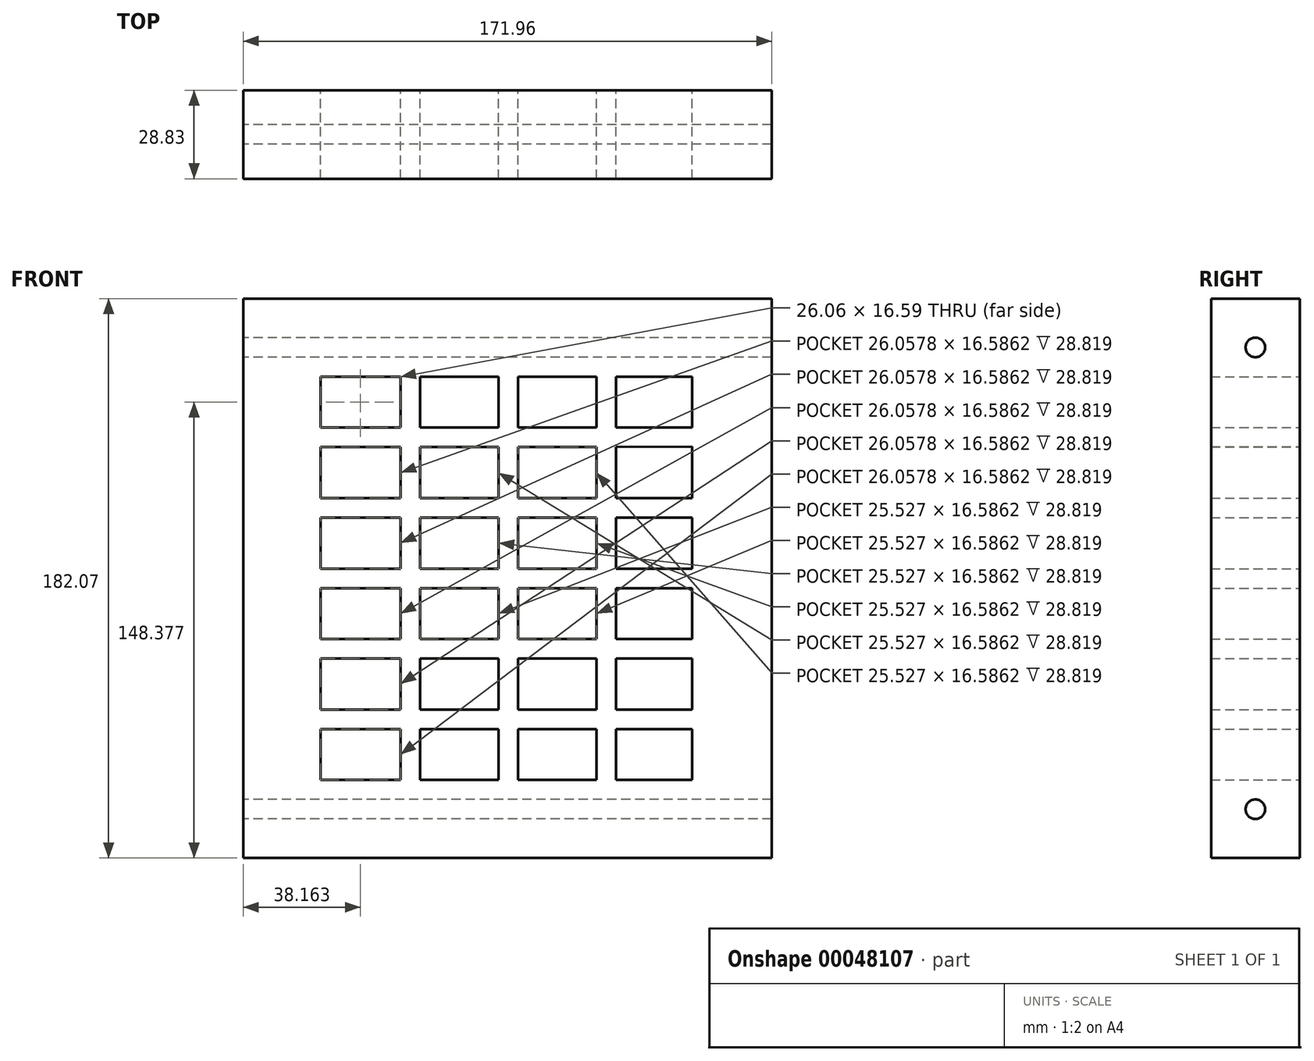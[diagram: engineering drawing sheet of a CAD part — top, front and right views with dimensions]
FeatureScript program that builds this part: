
annotation { "Feature Type Name" : "Feature", "Feature Type Description" : "" }
export const myFeature = defineFeature(function(context is Context, id is Id, definition is map)
    precondition{}
    {
        {
            var Q0;
            Q0=qCreatedBy(makeId("Front.planeOp"),FACE);
            var sketch = newSketch(context, id + "F0", { "sketchPlane" : qUnion([Q0])});
            skLineSegment(sketch, "E0", {"start": v(0, 0) * mm, "end": v(0, -182.07) * mm});
            skLineSegment(sketch, "E1", {"start": v(0, 0) * mm, "end": v(171.96, 0) * mm});
            skLineSegment(sketch, "E2", {"start": v(171.96, 0) * mm, "end": v(171.96, -182.07) * mm});
            skLineSegment(sketch, "E3", {"start": v(171.96, -182.07) * mm, "end": v(0, -182.07) * mm});
            skLineSegment(sketch, "E4", {"start": v(25.13, -25.4) * mm, "end": v(146.03, -25.4) * mm});
            skLineSegment(sketch, "E5.bottom", {"start": v(25.13, -25.4) * mm, "end": v(51.2, -25.4) * mm});
            skLineSegment(sketch, "E5.left", {"start": v(25.13, -25.4) * mm, "end": v(25.13, -41.46) * mm});
            skLineSegment(sketch, "E6", {"start": v(25.13, -25.4) * mm, "end": v(25.13, -41.99) * mm});
            skLineSegment(sketch, "E7", {"start": v(38.16, -48.34) * mm, "end": v(25.13, -48.34) * mm});
            skLineSegment(sketch, "E8", {"start": v(25.13, -48.34) * mm, "end": v(51.2, -48.34) * mm});
            skLineSegment(sketch, "E9", {"start": v(25.13, -48.34) * mm, "end": v(25.13, -64.92) * mm});
            skLineSegment(sketch, "E10", {"start": v(25.13, -41.99) * mm, "end": v(25.13, -48.34) * mm});
            skLineSegment(sketch, "E11", {"start": v(25.13, -64.92) * mm, "end": v(51.2, -64.92) * mm});
            skLineSegment(sketch, "E12", {"start": v(51.2, -64.92) * mm, "end": v(38.16, -64.92) * mm});
            skLineSegment(sketch, "E13", {"start": v(38.16, -71.27) * mm, "end": v(25.13, -71.27) * mm});
            skLineSegment(sketch, "E14", {"start": v(25.13, -71.27) * mm, "end": v(25.13, -87.86) * mm});
            skLineSegment(sketch, "E15", {"start": v(38.16, -71.27) * mm, "end": v(51.2, -71.27) * mm});
            skLineSegment(sketch, "E16", {"start": v(25.13, -87.86) * mm, "end": v(51.2, -87.86) * mm});
            skLineSegment(sketch, "E17", {"start": v(51.2, -87.86) * mm, "end": v(38.16, -87.86) * mm});
            skLineSegment(sketch, "E18", {"start": v(38.16, -94.2) * mm, "end": v(25.13, -94.2) * mm});
            skLineSegment(sketch, "E19", {"start": v(25.13, -94.2) * mm, "end": v(25.13, -110.8) * mm});
            skLineSegment(sketch, "E20", {"start": v(25.13, -110.8) * mm, "end": v(51.2, -110.8) * mm});
            skLineSegment(sketch, "E21", {"start": v(38.16, -94.2) * mm, "end": v(51.2, -94.2) * mm});
            skLineSegment(sketch, "E22", {"start": v(51.2, -94.2) * mm, "end": v(51.2, -110.8) * mm});
            skLineSegment(sketch, "E23", {"start": v(38.16, -117.14) * mm, "end": v(25.13, -117.14) * mm});
            skLineSegment(sketch, "E24", {"start": v(25.13, -117.14) * mm, "end": v(51.2, -117.14) * mm});
            skLineSegment(sketch, "E25", {"start": v(25.13, -117.14) * mm, "end": v(25.13, -133.73) * mm});
            skLineSegment(sketch, "E26", {"start": v(25.13, -133.73) * mm, "end": v(51.2, -133.73) * mm});
            skLineSegment(sketch, "E27", {"start": v(51.2, -133.73) * mm, "end": v(38.16, -133.73) * mm});
            skLineSegment(sketch, "E28", {"start": v(38.16, -140.08) * mm, "end": v(25.13, -140.08) * mm});
            skLineSegment(sketch, "E29", {"start": v(25.13, -140.08) * mm, "end": v(25.13, -156.67) * mm});
            skLineSegment(sketch, "E30", {"start": v(38.16, -140.08) * mm, "end": v(51.2, -140.08) * mm});
            skLineSegment(sketch, "E31", {"start": v(25.13, -25.4) * mm, "end": v(25.13, -156.67) * mm});
            skPoint(sketch, "E32.endSnap0", {"position": v(171.96, -91.03) * mm});
            skLineSegment(sketch, "E33", {"start": v(51.2, -25.4) * mm, "end": v(85.58, -25.4) * mm});
            skLineSegment(sketch, "E34", {"start": v(146.03, -25.4) * mm, "end": v(146.03, -156.67) * mm});
            skLineSegment(sketch, "E35", {"start": v(25.13, -156.67) * mm, "end": v(146.03, -156.67) * mm});
            skLineSegment(sketch, "E36", {"start": v(57.54, -140.08) * mm, "end": v(83.07, -140.08) * mm});
            skLineSegment(sketch, "E37", {"start": v(89.42, -140.08) * mm, "end": v(114.95, -140.08) * mm});
            skLineSegment(sketch, "E38", {"start": v(121.3, -140.08) * mm, "end": v(146.03, -140.08) * mm});
            skLineSegment(sketch, "E39", {"start": v(57.54, -117.14) * mm, "end": v(83.07, -117.14) * mm});
            skLineSegment(sketch, "E40", {"start": v(89.42, -117.14) * mm, "end": v(114.95, -117.14) * mm});
            skLineSegment(sketch, "E41", {"start": v(121.3, -117.14) * mm, "end": v(146.03, -117.14) * mm});
            skLineSegment(sketch, "E42", {"start": v(57.54, -94.2) * mm, "end": v(83.07, -94.2) * mm});
            skLineSegment(sketch, "E43", {"start": v(89.42, -94.2) * mm, "end": v(114.95, -94.2) * mm});
            skLineSegment(sketch, "E44", {"start": v(121.3, -94.2) * mm, "end": v(146.03, -94.2) * mm});
            skLineSegment(sketch, "E45", {"start": v(57.54, -87.86) * mm, "end": v(83.07, -87.86) * mm});
            skLineSegment(sketch, "E46", {"start": v(89.42, -87.86) * mm, "end": v(114.95, -87.86) * mm});
            skLineSegment(sketch, "E47", {"start": v(121.3, -87.86) * mm, "end": v(146.03, -87.86) * mm});
            skLineSegment(sketch, "E48", {"start": v(57.54, -71.27) * mm, "end": v(83.07, -71.27) * mm});
            skLineSegment(sketch, "E49", {"start": v(89.42, -71.27) * mm, "end": v(114.95, -71.27) * mm});
            skLineSegment(sketch, "E50", {"start": v(121.3, -71.27) * mm, "end": v(146.03, -71.27) * mm});
            skLineSegment(sketch, "E51", {"start": v(57.54, -110.8) * mm, "end": v(83.07, -110.8) * mm});
            skLineSegment(sketch, "E52", {"start": v(89.42, -110.8) * mm, "end": v(114.95, -110.8) * mm});
            skLineSegment(sketch, "E53", {"start": v(121.3, -110.8) * mm, "end": v(146.03, -110.8) * mm});
            skLineSegment(sketch, "E54", {"start": v(57.54, -133.73) * mm, "end": v(83.07, -133.73) * mm});
            skLineSegment(sketch, "E55", {"start": v(89.42, -133.73) * mm, "end": v(114.95, -133.73) * mm});
            skLineSegment(sketch, "E56", {"start": v(121.3, -133.73) * mm, "end": v(146.03, -133.73) * mm});
            skLineSegment(sketch, "E57", {"start": v(57.54, -64.92) * mm, "end": v(83.07, -64.92) * mm});
            skLineSegment(sketch, "E58", {"start": v(89.42, -64.92) * mm, "end": v(114.95, -64.92) * mm});
            skLineSegment(sketch, "E59", {"start": v(121.3, -64.92) * mm, "end": v(146.03, -64.92) * mm});
            skLineSegment(sketch, "E60", {"start": v(57.54, -48.34) * mm, "end": v(83.07, -48.34) * mm});
            skLineSegment(sketch, "E61", {"start": v(89.42, -48.34) * mm, "end": v(114.95, -48.34) * mm});
            skLineSegment(sketch, "E62", {"start": v(121.3, -48.34) * mm, "end": v(146.03, -48.2) * mm});
            skLineSegment(sketch, "E63", {"start": v(57.54, -41.99) * mm, "end": v(83.07, -41.99) * mm});
            skLineSegment(sketch, "E64", {"start": v(89.42, -41.99) * mm, "end": v(114.95, -41.99) * mm});
            skLineSegment(sketch, "E65", {"start": v(121.3, -41.99) * mm, "end": v(146.03, -41.99) * mm});
            skLineSegment(sketch, "E66", {"start": v(51.2, -140.08) * mm, "end": v(51.2, -156.67) * mm});
            skLineSegment(sketch, "E67", {"start": v(51.2, -117.14) * mm, "end": v(51.2, -133.73) * mm});
            skLineSegment(sketch, "E68", {"start": v(51.2, -87.86) * mm, "end": v(51.2, -71.27) * mm});
            skLineSegment(sketch, "E69", {"start": v(51.2, -64.92) * mm, "end": v(51.2, -48.34) * mm});
            skLineSegment(sketch, "E70", {"start": v(57.54, -41.99) * mm, "end": v(57.54, -25.4) * mm});
            skLineSegment(sketch, "E71", {"start": v(57.54, -48.34) * mm, "end": v(57.54, -64.92) * mm});
            skLineSegment(sketch, "E72", {"start": v(57.54, -71.27) * mm, "end": v(57.54, -87.86) * mm});
            skLineSegment(sketch, "E73", {"start": v(57.54, -94.2) * mm, "end": v(57.54, -110.8) * mm});
            skLineSegment(sketch, "E74", {"start": v(57.54, -117.14) * mm, "end": v(57.54, -133.73) * mm});
            skLineSegment(sketch, "E75", {"start": v(57.54, -140.08) * mm, "end": v(57.54, -156.67) * mm});
            skLineSegment(sketch, "E76", {"start": v(83.07, -140.08) * mm, "end": v(83.07, -156.67) * mm});
            skLineSegment(sketch, "E77", {"start": v(83.07, -133.73) * mm, "end": v(83.07, -117.14) * mm});
            skLineSegment(sketch, "E78", {"start": v(83.07, -110.8) * mm, "end": v(83.07, -94.2) * mm});
            skLineSegment(sketch, "E79", {"start": v(83.07, -87.86) * mm, "end": v(83.07, -71.27) * mm});
            skLineSegment(sketch, "E80", {"start": v(83.07, -64.92) * mm, "end": v(83.07, -48.34) * mm});
            skLineSegment(sketch, "E81", {"start": v(83.07, -41.99) * mm, "end": v(83.07, -25.4) * mm});
            skLineSegment(sketch, "E82", {"start": v(89.42, -41.99) * mm, "end": v(89.42, -25.4) * mm});
            skLineSegment(sketch, "E83", {"start": v(89.42, -48.34) * mm, "end": v(89.42, -64.92) * mm});
            skLineSegment(sketch, "E84", {"start": v(89.42, -87.86) * mm, "end": v(89.42, -71.27) * mm});
            skLineSegment(sketch, "E85", {"start": v(89.42, -94.2) * mm, "end": v(89.42, -110.8) * mm});
            skLineSegment(sketch, "E86", {"start": v(89.42, -117.14) * mm, "end": v(89.42, -133.73) * mm});
            skLineSegment(sketch, "E87", {"start": v(89.42, -140.08) * mm, "end": v(89.42, -156.67) * mm});
            skLineSegment(sketch, "E88", {"start": v(114.95, -140.08) * mm, "end": v(114.95, -156.67) * mm});
            skLineSegment(sketch, "E89", {"start": v(114.95, -133.73) * mm, "end": v(114.95, -117.14) * mm});
            skLineSegment(sketch, "E90", {"start": v(114.95, -110.8) * mm, "end": v(114.95, -94.2) * mm});
            skLineSegment(sketch, "E91", {"start": v(114.95, -87.86) * mm, "end": v(114.95, -71.27) * mm});
            skLineSegment(sketch, "E92", {"start": v(114.95, -64.92) * mm, "end": v(114.95, -48.34) * mm});
            skLineSegment(sketch, "E93", {"start": v(114.95, -41.99) * mm, "end": v(114.95, -25.4) * mm});
            skLineSegment(sketch, "E94", {"start": v(121.3, -41.99) * mm, "end": v(121.3, -25.4) * mm});
            skLineSegment(sketch, "E95", {"start": v(121.3, -48.34) * mm, "end": v(121.3, -64.92) * mm});
            skLineSegment(sketch, "E96", {"start": v(121.3, -71.27) * mm, "end": v(121.3, -87.86) * mm});
            skLineSegment(sketch, "E97", {"start": v(121.3, -94.2) * mm, "end": v(121.3, -110.8) * mm});
            skLineSegment(sketch, "E98", {"start": v(121.3, -117.14) * mm, "end": v(121.3, -133.73) * mm});
            skLineSegment(sketch, "E99", {"start": v(121.3, -140.08) * mm, "end": v(121.3, -156.67) * mm});
            skLineSegment(sketch, "E100", {"start": v(25.13, -41.99) * mm, "end": v(51.2, -41.99) * mm});
            skLineSegment(sketch, "E101", {"start": v(51.2, -41.99) * mm, "end": v(51.2, -25.4) * mm});
            skSolve(sketch);
        }
        {
            var Q0;
            Q0=makeQuery(id+"F0.imprint","IMPRINT",FACE,{"disambiguationData":[TD([[makeQuery(id+"F0.imprint","IMPRINT",EDGE,{"derivedFrom":sQuery(id+"F0.wireOp",EDGE,"E0")}),1.0]])]});
            var Q1;
            {var subQ22=sQuery(id+"F0.wireOp",EDGE,"E11");Q1=makeQuery(id+"F0.imprint","IMPRINT",FACE,{"disambiguationData":[TD([[makeQuery(id+"F0.imprint","IMPRINT",EDGE,{"derivedFrom":subQ22}),-1.0]])]});}
            var Q2;
            Q2=qCreatedBy(makeId("Front.planeOp"),FACE);
            extrude(context, id + "F1", {"entities" : qUnion([Q0, Q1]), "endBoundEntityFace" : qUnion([Q2]), "depth" : 28.83 * mm});
        }
        {
            var Q0;
            {var subQ2=sQuery(id+"F0.wireOp",EDGE,"E5.bottom");Q0=makeQuery(id+"F0.imprint","IMPRINT",FACE,{"disambiguationData":[TD([[makeQuery(id+"F0.imprint","IMPRINT",EDGE,{"derivedFrom":subQ2}),-1.0]])]});}
            var Q1;
            Q1=makeQuery(id+"F0.imprint","IMPRINT",FACE,{"disambiguationData":[TD([[makeQuery(id+"F0.imprint","IMPRINT",EDGE,{"derivedFrom":sQuery(id+"F0.wireOp",EDGE,"E63")}),1.0]])]});
            var Q2;
            Q2=makeQuery(id+"F0.imprint","IMPRINT",FACE,{"disambiguationData":[TD([[makeQuery(id+"F0.imprint","IMPRINT",EDGE,{"derivedFrom":sQuery(id+"F0.wireOp",EDGE,"E64")}),1.0]])]});
            var Q3;
            {var subQ0=sQuery(id+"F0.wireOp",EDGE,"E65");Q3=makeQuery(id+"F0.imprint","IMPRINT",FACE,{"disambiguationData":[TD([[makeQuery(id+"F0.imprint","IMPRINT",EDGE,{"derivedFrom":subQ0}),1.0]])]});}
            var Q4;
            {var subQ1=sQuery(id+"F0.wireOp",EDGE,"E59");Q4=makeQuery(id+"F0.imprint","IMPRINT",FACE,{"disambiguationData":[TD([[makeQuery(id+"F0.imprint","IMPRINT",EDGE,{"derivedFrom":subQ1}),1.0]])]});}
            var Q5;
            Q5=makeQuery(id+"F0.imprint","IMPRINT",FACE,{"disambiguationData":[TD([[makeQuery(id+"F0.imprint","IMPRINT",EDGE,{"derivedFrom":sQuery(id+"F0.wireOp",EDGE,"E58")}),1.0]])]});
            var Q6;
            Q6=makeQuery(id+"F0.imprint","IMPRINT",FACE,{"disambiguationData":[TD([[makeQuery(id+"F0.imprint","IMPRINT",EDGE,{"derivedFrom":sQuery(id+"F0.wireOp",EDGE,"E57")}),1.0]])]});
            var Q7;
            {var subQ5=sQuery(id+"F0.wireOp",EDGE,"E11");Q7=makeQuery(id+"F0.imprint","IMPRINT",FACE,{"disambiguationData":[TD([[makeQuery(id+"F0.imprint","IMPRINT",EDGE,{"derivedFrom":subQ5}),1.0]])]});}
            var Q8;
            {var subQ2=sQuery(id+"F0.wireOp",EDGE,"E13");Q8=makeQuery(id+"F0.imprint","IMPRINT",FACE,{"disambiguationData":[TD([[makeQuery(id+"F0.imprint","IMPRINT",EDGE,{"derivedFrom":subQ2}),1.0]])]});}
            var Q9;
            Q9=makeQuery(id+"F0.imprint","IMPRINT",FACE,{"disambiguationData":[TD([[makeQuery(id+"F0.imprint","IMPRINT",EDGE,{"derivedFrom":sQuery(id+"F0.wireOp",EDGE,"E45")}),1.0]])]});
            var Q10;
            Q10=makeQuery(id+"F0.imprint","IMPRINT",FACE,{"disambiguationData":[TD([[makeQuery(id+"F0.imprint","IMPRINT",EDGE,{"derivedFrom":sQuery(id+"F0.wireOp",EDGE,"E46")}),1.0]])]});
            var Q11;
            {var subQ1=sQuery(id+"F0.wireOp",EDGE,"E47");Q11=makeQuery(id+"F0.imprint","IMPRINT",FACE,{"disambiguationData":[TD([[makeQuery(id+"F0.imprint","IMPRINT",EDGE,{"derivedFrom":subQ1}),1.0]])]});}
            var Q12;
            {var subQ1=sQuery(id+"F0.wireOp",EDGE,"E44");Q12=makeQuery(id+"F0.imprint","IMPRINT",FACE,{"disambiguationData":[TD([[makeQuery(id+"F0.imprint","IMPRINT",EDGE,{"derivedFrom":subQ1}),-1.0]])]});}
            var Q13;
            Q13=makeQuery(id+"F0.imprint","IMPRINT",FACE,{"disambiguationData":[TD([[makeQuery(id+"F0.imprint","IMPRINT",EDGE,{"derivedFrom":sQuery(id+"F0.wireOp",EDGE,"E43")}),-1.0]])]});
            var Q14;
            Q14=makeQuery(id+"F0.imprint","IMPRINT",FACE,{"disambiguationData":[TD([[makeQuery(id+"F0.imprint","IMPRINT",EDGE,{"derivedFrom":sQuery(id+"F0.wireOp",EDGE,"E42")}),-1.0]])]});
            var Q15;
            {var subQ2=sQuery(id+"F0.wireOp",EDGE,"E18");Q15=makeQuery(id+"F0.imprint","IMPRINT",FACE,{"disambiguationData":[TD([[makeQuery(id+"F0.imprint","IMPRINT",EDGE,{"derivedFrom":subQ2}),1.0]])]});}
            var Q16;
            {var subQ2=sQuery(id+"F0.wireOp",EDGE,"E26");Q16=makeQuery(id+"F0.imprint","IMPRINT",FACE,{"disambiguationData":[TD([[makeQuery(id+"F0.imprint","IMPRINT",EDGE,{"derivedFrom":subQ2}),1.0]])]});}
            var Q17;
            {var subQ1=sQuery(id+"F0.wireOp",EDGE,"E41");Q17=makeQuery(id+"F0.imprint","IMPRINT",FACE,{"disambiguationData":[TD([[makeQuery(id+"F0.imprint","IMPRINT",EDGE,{"derivedFrom":subQ1}),-1.0]])]});}
            var Q18;
            {var subQ1=sQuery(id+"F0.wireOp",EDGE,"E38");Q18=makeQuery(id+"F0.imprint","IMPRINT",FACE,{"disambiguationData":[TD([[makeQuery(id+"F0.imprint","IMPRINT",EDGE,{"derivedFrom":subQ1}),-1.0]])]});}
            var Q19;
            Q19=makeQuery(id+"F0.imprint","IMPRINT",FACE,{"disambiguationData":[TD([[makeQuery(id+"F0.imprint","IMPRINT",EDGE,{"derivedFrom":sQuery(id+"F0.wireOp",EDGE,"E37")}),-1.0]])]});
            var Q20;
            Q20=makeQuery(id+"F0.imprint","IMPRINT",FACE,{"disambiguationData":[TD([[makeQuery(id+"F0.imprint","IMPRINT",EDGE,{"derivedFrom":sQuery(id+"F0.wireOp",EDGE,"E36")}),-1.0]])]});
            var Q21;
            {var subQ0=sQuery(id+"F0.wireOp",EDGE,"E28");Q21=makeQuery(id+"F0.imprint","IMPRINT",FACE,{"disambiguationData":[TD([[makeQuery(id+"F0.imprint","IMPRINT",EDGE,{"derivedFrom":subQ0}),1.0]])]});}
            var Q22;
            Q22=makeQuery(id+"F0.imprint","IMPRINT",FACE,{"disambiguationData":[TD([[makeQuery(id+"F0.imprint","IMPRINT",EDGE,{"derivedFrom":sQuery(id+"F0.wireOp",EDGE,"E40")}),-1.0]])]});
            var Q23;
            Q23=makeQuery(id+"F0.imprint","IMPRINT",FACE,{"disambiguationData":[TD([[makeQuery(id+"F0.imprint","IMPRINT",EDGE,{"derivedFrom":sQuery(id+"F0.wireOp",EDGE,"E40")}),-1.0]])]});
            var Q24;
            Q24=makeQuery(id+"F0.imprint","IMPRINT",FACE,{"disambiguationData":[TD([[makeQuery(id+"F0.imprint","IMPRINT",EDGE,{"derivedFrom":sQuery(id+"F0.wireOp",EDGE,"E39")}),-1.0]])]});
            extrude(context, id + "F2", {"entities" : qUnion([Q0, Q1, Q2, Q3, Q4, Q5, Q6, Q7, Q8, Q9, Q10, Q11, Q12, Q13, Q14, Q15, Q16, Q17, Q18, Q19, Q20, Q21, Q22, Q23, Q24]), "operationType" : NewBodyOperationType.ADD, "depth" : 1 / 101.6 * mm});
        }
        {
            var Q0;
            Q0=makeQuery(id+"F1.opExtrude","SWEPT_FACE",FACE,{"disambiguationData":[OSD([sQuery(id+"F0.wireOp",EDGE,"E0")])]});
            var sketch = newSketch(context, id + "F3", { "sketchPlane" : qUnion([Q0])});
            skCircle(sketch, "E102", {"center": v(14.41, -15.88) * mm, "radius": 3.17 * mm});
            skCircle(sketch, "E103", {"center": v(14.41, -166.2) * mm, "radius": 3.18 * mm});
            skSolve(sketch);
        }
        {
            var Q0;
            Q0 = qSketchRegion(id + "F3", true);
            extrude(context, id + "F4", {"entities" : qUnion([Q0]), "operationType" : NewBodyOperationType.REMOVE, "oppositeDirection" : true, "depth" : 203.2 * mm});
        }
    });
